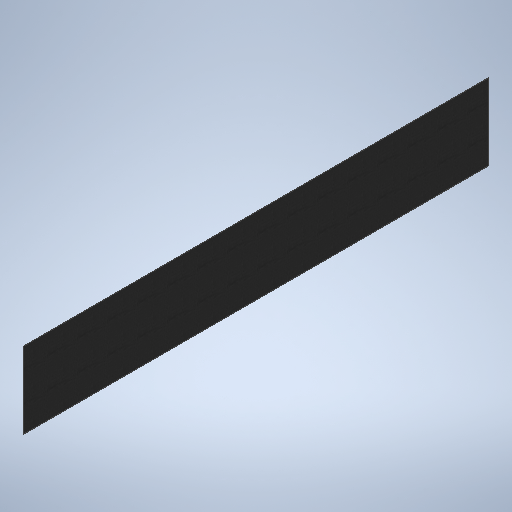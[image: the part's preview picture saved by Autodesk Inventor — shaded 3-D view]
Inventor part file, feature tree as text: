
AUTODESK INVENTOR PART (.ipt)
format: ipt  version: 2025.1 (Build 291241020, 241B)  size: 253,952 bytes
history: native  units: in
note: dims shown in document units (in); Inventor stores cm internally (conversion verified against a paired STEP export)
features: extrude x1, sketch x1
ambient origin geometry x8: Origin, YZ Plane, XZ Plane, XY Plane, X Axis, Y Axis, Z Axis, Center Point
bodies: Solid1 (feature_tree)
feature tree (2):
  extrude  "Extrusion1"  Depth=292.513in
  sketch  "Sketch1"  dims[d2=0.125in d3=0.0in d4=292.513in d5=48.0in]
